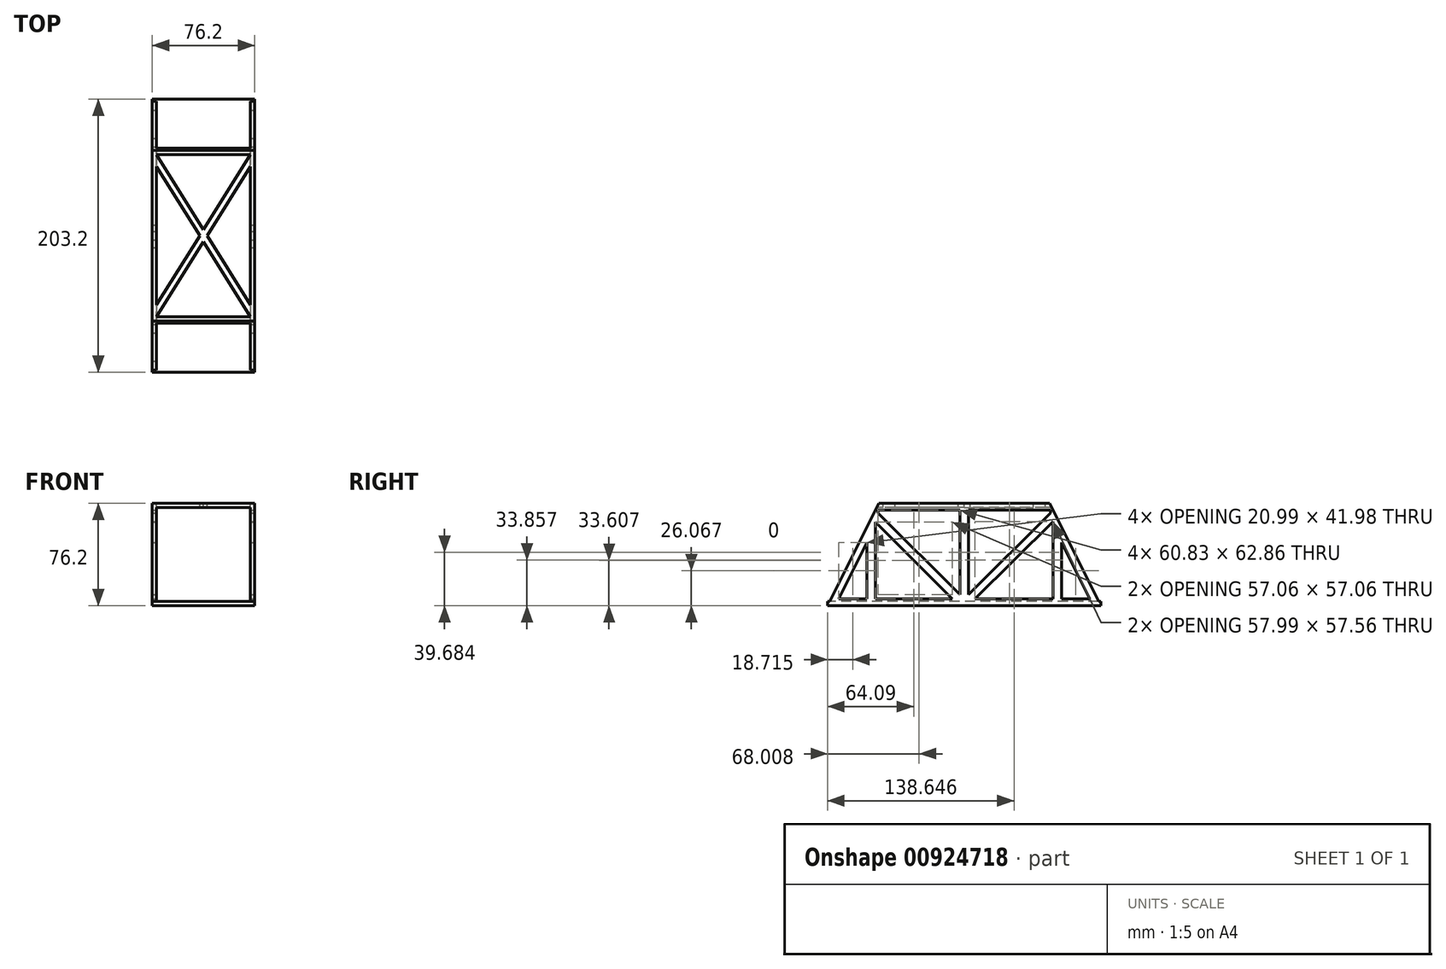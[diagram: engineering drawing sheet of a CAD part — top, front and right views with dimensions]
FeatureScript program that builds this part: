
annotation { "Feature Type Name" : "Feature", "Feature Type Description" : "" }
export const myFeature = defineFeature(function(context is Context, id is Id, definition is map)
    precondition{}
    {
        {
            var Q0;
            Q0=qCreatedBy(makeId("Right.planeOp"),FACE);
            var sketch = newSketch(context, id + "F0", { "sketchPlane" : qUnion([Q0])});
            skLineSegment(sketch, "E0", {"start": v(-101.6, -44.1) * mm, "end": v(101.6, -44.1) * mm});
            skLineSegment(sketch, "E1", {"start": v(-63.5, 32.1) * mm, "end": v(63.5, 32.1) * mm});
            skLineSegment(sketch, "E2", {"start": v(-101.6, -44.1) * mm, "end": v(-63.5, 32.1) * mm});
            skLineSegment(sketch, "E3", {"start": v(63.5, 32.1) * mm, "end": v(101.6, -44.1) * mm});
            skSolve(sketch);
        }
        {
            var Q0;
            Q0=makeQuery(id+"F0.imprint","IMPRINT",FACE,{"disambiguationData":[TD([[makeQuery(id+"F0.imprint","IMPRINT",EDGE,{"derivedFrom":sQuery(id+"F0.wireOp",EDGE,"E0")}),1.0]])]});
            extrude(context, id + "F1", {"entities" : qUnion([Q0]), "endBound" : BoundingType.SYMMETRIC, "depth" : 76.2 * mm, "offsetDistance" : 25.4 * mm});
        }
        {
            var Q0;
            Q0=qCreatedBy(makeId("Front.planeOp"),FACE);
            var sketch = newSketch(context, id + "F2", { "sketchPlane" : qUnion([Q0])});
            skLineSegment(sketch, "E4.bottom", {"start": v(34.92, -40.93) * mm, "end": v(-34.93, -40.93) * mm});
            skLineSegment(sketch, "E4.top", {"start": v(34.92, 28.92) * mm, "end": v(-34.92, 28.92) * mm});
            skLineSegment(sketch, "E4.left", {"start": v(34.93, -40.93) * mm, "end": v(34.93, 28.92) * mm});
            skLineSegment(sketch, "E4.right", {"start": v(-34.93, -40.93) * mm, "end": v(-34.93, 28.92) * mm});
            skPoint(sketch, "E4.middle", {"position": v(0, -6) * mm});
            skSolve(sketch);
        }
        {
            var Q0;
            Q0=qSketchRegion(id+"F2",true);
            extrude(context, id + "F3", {"entities" : qUnion([Q0]), "operationType" : NewBodyOperationType.REMOVE, "endBound" : BoundingType.SYMMETRIC, "oppositeDirection" : true, "depth" : 254 * mm, "offsetDistance" : 25.4 * mm});
        }
        {
            var Q0;
            Q0=makeQuery(id+"F1.opExtrude","CAP_FACE",FACE,{"disambiguationData":[OSD([sQuery(id+"F0.wireOp",EDGE,"E0"),sQuery(id+"F0.wireOp",EDGE,"E1"),sQuery(id+"F0.wireOp",EDGE,"E2"),sQuery(id+"F0.wireOp",EDGE,"E3")])],"isStart":false});
            var sketch = newSketch(context, id + "F4", { "sketchPlane" : qUnion([Q0])});
            skLineSegment(sketch, "E5", {"start": v(-99.06, -39.02) * mm, "end": v(99.06, -39.02) * mm});
            skLineSegment(sketch, "E6", {"start": v(-66.04, 27.02) * mm, "end": v(66.04, 27.02) * mm});
            skLineSegment(sketch, "E7", {"start": v(-66.04, 27.02) * mm, "end": v(-66.04, -39.02) * mm});
            skLineSegment(sketch, "E8", {"start": v(66.04, 27.02) * mm, "end": v(66.04, -39.02) * mm});
            skLineSegment(sketch, "E9", {"start": v(-72.4, 14.32) * mm, "end": v(-72.4, -39.02) * mm});
            skLineSegment(sketch, "E10", {"start": v(72.39, 14.32) * mm, "end": v(72.39, -39.02) * mm});
            skLineSegment(sketch, "E11", {"start": v(72.39, 2.96) * mm, "end": v(93.38, -39.02) * mm});
            skLineSegment(sketch, "E12", {"start": v(-72.4, 2.96) * mm, "end": v(-93.38, -39.02) * mm});
            skLineSegment(sketch, "E13", {"start": v(-66.04, 27.02) * mm, "end": v(0, -39.02) * mm});
            skLineSegment(sketch, "E14", {"start": v(0, -39.02) * mm, "end": v(66.04, 27.02) * mm});
            skLineSegment(sketch, "E15", {"start": v(-66.04, 18.04) * mm, "end": v(-8, -40) * mm});
            skLineSegment(sketch, "E16", {"start": v(8.05, -39.02) * mm, "end": v(66.04, 18.54) * mm});
            skLineSegment(sketch, "E17", {"start": v(-3.18, 27.02) * mm, "end": v(-3.17, -35.85) * mm});
            skLineSegment(sketch, "E18", {"start": v(3.17, 27.02) * mm, "end": v(3.18, -35.85) * mm});
            skLineSegment(sketch, "E19", {"start": v(-64, 27.02) * mm, "end": v(-64, 24.99) * mm});
            skLineSegment(sketch, "E20", {"start": v(64, 27.02) * mm, "end": v(64, 24.99) * mm});
            skSolve(sketch);
        }
        {
            var Q0;
            {var subQ3=sQuery(id+"F4.wireOp",EDGE,"E12");Q0=makeQuery(id+"F4.imprint","IMPRINT",FACE,{"disambiguationData":[TD([[makeQuery(id+"F4.imprint","IMPRINT",EDGE,{"derivedFrom":subQ3}),1.0]])]});}
            var Q1;
            {var subQ0=sQuery(id+"F4.wireOp",EDGE,"E7");var subQ1=sQuery(id+"F4.wireOp",EDGE,"E5");var subQ2=makeQuery(id+"F4.imprint","INTERSECT",VERTEX,{"derivedFrom":[subQ1,subQ0]});Q1=makeQuery(id+"F4.imprint","IMPRINT",FACE,{"disambiguationData":[TD([[makeQuery(id+"F4.imprint","IMPRINT",EDGE,{"disambiguationData":[TD([[subQ2,-1.0]])],"derivedFrom":subQ1}),1.0]])]});}
            var Q2;
            {var subQ0=sQuery(id+"F4.wireOp",EDGE,"E17");Q2=makeQuery(id+"F4.imprint","IMPRINT",FACE,{"disambiguationData":[TD([[makeQuery(id+"F4.imprint","IMPRINT",EDGE,{"derivedFrom":subQ0}),-1.0]])]});}
            var Q3;
            {var subQ0=sQuery(id+"F4.wireOp",EDGE,"E18");Q3=makeQuery(id+"F4.imprint","IMPRINT",FACE,{"disambiguationData":[TD([[makeQuery(id+"F4.imprint","IMPRINT",EDGE,{"derivedFrom":subQ0}),1.0]])]});}
            var Q4;
            {var subQ3=sQuery(id+"F4.wireOp",EDGE,"E16");Q4=makeQuery(id+"F4.imprint","IMPRINT",FACE,{"disambiguationData":[TD([[makeQuery(id+"F4.imprint","IMPRINT",EDGE,{"derivedFrom":subQ3}),-1.0]])]});}
            var Q5;
            {var subQ3=sQuery(id+"F4.wireOp",EDGE,"E11");Q5=makeQuery(id+"F4.imprint","IMPRINT",FACE,{"disambiguationData":[TD([[makeQuery(id+"F4.imprint","IMPRINT",EDGE,{"derivedFrom":subQ3}),-1.0]])]});}
            extrude(context, id + "F5", {"entities" : qUnion([Q0, Q1, Q2, Q3, Q4, Q5]), "operationType" : NewBodyOperationType.REMOVE, "oppositeDirection" : true, "depth" : 76.2 * mm, "offsetDistance" : 25.4 * mm});
        }
        {
            var Q0;
            Q0=makeQuery(id+"F1.opExtrude","SWEPT_FACE",FACE,{"disambiguationData":[OSD([sQuery(id+"F0.wireOp",EDGE,"E1")])]});
            var sketch = newSketch(context, id + "F6", { "sketchPlane" : qUnion([Q0])});
            skLineSegment(sketch, "E21.bottom", {"start": v(34.92, -60.32) * mm, "end": v(-34.92, -60.33) * mm});
            skLineSegment(sketch, "E21.top", {"start": v(34.92, 60.33) * mm, "end": v(-34.92, 60.33) * mm});
            skLineSegment(sketch, "E21.left", {"start": v(34.92, -60.33) * mm, "end": v(34.92, 60.33) * mm});
            skLineSegment(sketch, "E21.right", {"start": v(-34.92, -60.33) * mm, "end": v(-34.92, 60.33) * mm});
            skPoint(sketch, "E21.middle", {"position": v(0, 0) * mm});
            skLineSegment(sketch, "E22", {"start": v(-34.92, 51.44) * mm, "end": v(34.93, -60.33) * mm});
            skLineSegment(sketch, "E23", {"start": v(-34.92, 60.33) * mm, "end": v(34.92, -51.44) * mm});
            skLineSegment(sketch, "E24", {"start": v(-34.93, -60.33) * mm, "end": v(34.93, 51.44) * mm});
            skLineSegment(sketch, "E25", {"start": v(-34.92, -51.44) * mm, "end": v(34.92, 60.33) * mm});
            skSolve(sketch);
        }
        {
            var Q0;
            {var subQ0=sQuery(id+"F6.wireOp",EDGE,"E22");var subQ1=sQuery(id+"F6.wireOp",EDGE,"E21.right");var subQ2=makeQuery(id+"F6.imprint","INTERSECT",VERTEX,{"derivedFrom":[subQ1,subQ0]});Q0=makeQuery(id+"F6.imprint","IMPRINT",FACE,{"disambiguationData":[TD([[makeQuery(id+"F6.imprint","IMPRINT",EDGE,{"disambiguationData":[TD([[subQ2,1.0]])],"derivedFrom":subQ1}),-1.0]])]});}
            var Q1;
            {var subQ0=sQuery(id+"F6.wireOp",EDGE,"E21.top");Q1=makeQuery(id+"F6.imprint","IMPRINT",FACE,{"disambiguationData":[TD([[makeQuery(id+"F6.imprint","IMPRINT",EDGE,{"derivedFrom":subQ0}),1.0]])]});}
            var Q2;
            {var subQ0=sQuery(id+"F6.wireOp",EDGE,"E23");var subQ1=sQuery(id+"F6.wireOp",EDGE,"E21.left");var subQ2=makeQuery(id+"F6.imprint","INTERSECT",VERTEX,{"derivedFrom":[subQ1,subQ0]});Q2=makeQuery(id+"F6.imprint","IMPRINT",FACE,{"disambiguationData":[TD([[makeQuery(id+"F6.imprint","IMPRINT",EDGE,{"disambiguationData":[TD([[subQ2,-1.0]])],"derivedFrom":subQ1}),1.0]])]});}
            var Q3;
            {var subQ0=sQuery(id+"F6.wireOp",EDGE,"E21.bottom");Q3=makeQuery(id+"F6.imprint","IMPRINT",FACE,{"disambiguationData":[TD([[makeQuery(id+"F6.imprint","IMPRINT",EDGE,{"derivedFrom":subQ0}),-1.0]])]});}
            extrude(context, id + "F7", {"entities" : qUnion([Q0, Q1, Q2, Q3]), "operationType" : NewBodyOperationType.REMOVE, "oppositeDirection" : true, "depth" : 5.6 * mm, "offsetDistance" : 25.4 * mm});
        }
        {
            var Q0;
            Q0=makeQuery(id+"F1.opExtrude","CAP_FACE",FACE,{"disambiguationData":[OSD([sQuery(id+"F0.wireOp",EDGE,"E0"),sQuery(id+"F0.wireOp",EDGE,"E1"),sQuery(id+"F0.wireOp",EDGE,"E2"),sQuery(id+"F0.wireOp",EDGE,"E3")])],"isStart":false});
            var sketch = newSketch(context, id + "F8", { "sketchPlane" : qUnion([Q0])});
            skLineSegment(sketch, "E26.bottom", {"start": v(-96.52, -40.93) * mm, "end": v(-101.6, -40.93) * mm});
            skLineSegment(sketch, "E26.top", {"start": v(-96.52, -44.1) * mm, "end": v(-101.6, -44.1) * mm});
            skLineSegment(sketch, "E26.left", {"start": v(-96.52, -40.93) * mm, "end": v(-96.52, -44.1) * mm});
            skLineSegment(sketch, "E26.right", {"start": v(-101.6, -40.93) * mm, "end": v(-101.6, -44.1) * mm});
            skLineSegment(sketch, "E27.MirrorCS", {"start": v(96.52, -40.93) * mm, "end": v(101.6, -40.93) * mm});
            skLineSegment(sketch, "E28.MirrorCS", {"start": v(96.52, -40.93) * mm, "end": v(96.52, -44.1) * mm});
            skLineSegment(sketch, "E29.MirrorCS", {"start": v(96.52, -44.1) * mm, "end": v(101.6, -44.1) * mm});
            skLineSegment(sketch, "E30.MirrorCS", {"start": v(101.6, -40.93) * mm, "end": v(101.6, -44.1) * mm});
            skSolve(sketch);
        }
        {
            var Q0;
            Q0=qSketchRegion(id+"F8",true);
            extrude(context, id + "F9", {"entities" : qUnion([Q0]), "operationType" : NewBodyOperationType.ADD, "oppositeDirection" : true, "depth" : 76.2 * mm, "offsetDistance" : 25.4 * mm});
        }
    });
